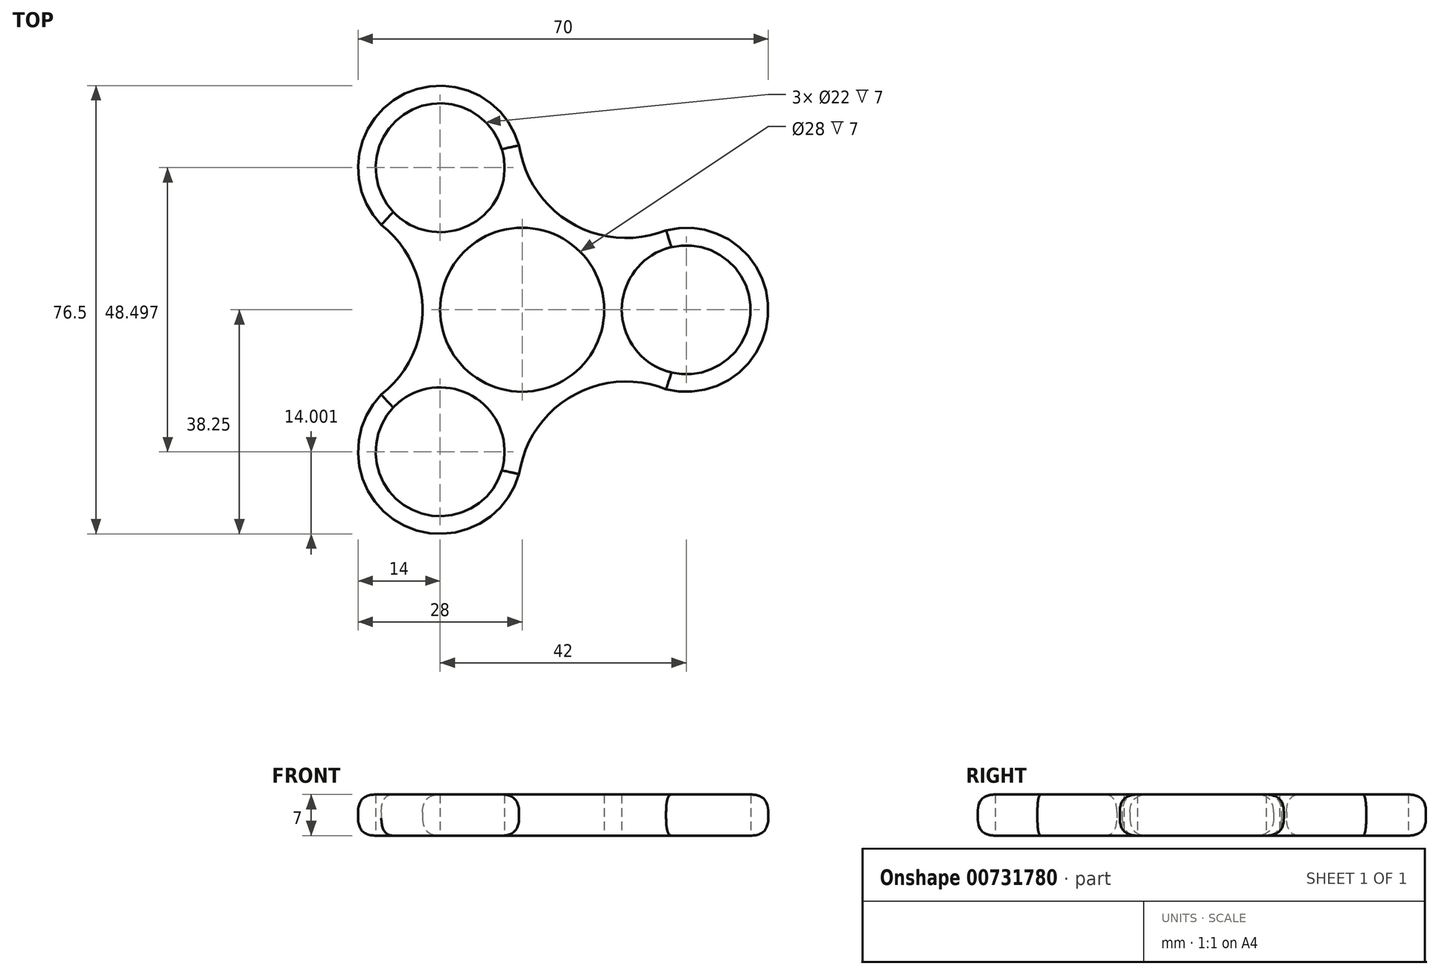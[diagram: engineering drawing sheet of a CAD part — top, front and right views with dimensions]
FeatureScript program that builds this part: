
annotation { "Feature Type Name" : "Feature", "Feature Type Description" : "" }
export const myFeature = defineFeature(function(context is Context, id is Id, definition is map)
    precondition{}
    {
        {
            var Q0;
            Q0=qCreatedBy(makeId("Top.planeOp"),FACE);
            var sketch = newSketch(context, id + "F0", { "sketchPlane" : qUnion([Q0])});
            skLineSegment(sketch, "E0", {"start": v(17, 0) * mm, "end": v(28, 0) * mm});
            skCircle(sketch, "E1", {"center": v(28, 0) * mm, "radius": 11 * mm});
            skArc(sketch, "E2", {"start": v(22.57, -12.9) * mm, "mid": v(42, 0) * mm, "end": v(22.57, 12.9) * mm});
            skPoint(sketch, "E3.center", {"position": v(0, 0) * mm});
            skArc(sketch, "E4", {"start": v(-24.03, -14.48) * mm, "mid": v(-17, 0) * mm, "end": v(-24.03, 14.48) * mm});
            skArc(sketch, "E5.1.0", {"start": v(24.56, -13.57) * mm, "mid": v(8.5, -14.72) * mm, "end": v(-0.53, -28.05) * mm});
            skArc(sketch, "E5.1.1", {"start": v(-0.1, 26) * mm, "mid": v(-21, 36.37) * mm, "end": v(-22.46, 13.1) * mm});
            skCircle(sketch, "E5.1.2", {"center": v(-14, 24.25) * mm, "radius": 11 * mm});
            skArc(sketch, "E5.2.0", {"start": v(-0.53, 28.05) * mm, "mid": v(8.5, 14.72) * mm, "end": v(24.56, 13.57) * mm});
            skArc(sketch, "E5.2.1", {"start": v(-22.46, -13.1) * mm, "mid": v(-21, -36.37) * mm, "end": v(-0.1, -26) * mm});
            skCircle(sketch, "E5.2.2", {"center": v(-14, -24.25) * mm, "radius": 11 * mm});
            skCircle(sketch, "E6", {"center": v(0, 0) * mm, "radius": 14 * mm});
            skSolve(sketch);
        }
        {
            var Q0;
            Q0=makeQuery(id+"F0.imprint","IMPRINT",FACE,{"disambiguationData":[TD([[makeQuery(id+"F0.imprint","IMPRINT",EDGE,{"derivedFrom":sQuery(id+"F0.wireOp",EDGE,"E1")}),-1.0]])]});
            extrude(context, id + "F1", {"entities" : qUnion([Q0]), "depth" : 3.5 * mm, "offsetDistance" : 25 * mm, "hasSecondDirection" : true, "secondDirectionOppositeDirection" : true, "secondDirectionDepth" : 3.5 * mm});
        }
        {
            var Q0;
            Q0=makeQuery(id+"F1.opExtrude","CAP_EDGE",EDGE,{"disambiguationData":[OSD([sQuery(id+"F0.wireOp",EDGE,"E5.1.0")])],"isStart":false});
            var Q1;
            Q1=makeQuery(id+"F1.opExtrude","CAP_EDGE",EDGE,{"disambiguationData":[OSD([sQuery(id+"F0.wireOp",EDGE,"E4")])],"isStart":false});
            var Q2;
            Q2=makeQuery(id+"F1.opExtrude","CAP_EDGE",EDGE,{"disambiguationData":[OSD([sQuery(id+"F0.wireOp",EDGE,"E5.2.0")])],"isStart":false});
            var Q3;
            Q3=makeQuery(id+"F1.opExtrude","CAP_EDGE",EDGE,{"disambiguationData":[OSD([sQuery(id+"F0.wireOp",EDGE,"E5.2.1")])],"isStart":false});
            var Q4;
            Q4=makeQuery(id+"F1.opExtrude","CAP_EDGE",EDGE,{"disambiguationData":[OSD([sQuery(id+"F0.wireOp",EDGE,"E2")])],"isStart":false});
            var Q5;
            Q5=makeQuery(id+"F1.opExtrude","CAP_EDGE",EDGE,{"disambiguationData":[OSD([sQuery(id+"F0.wireOp",EDGE,"E5.1.1")])],"isStart":false});
            var Q6;
            Q6=makeQuery(id+"F1.opExtrude","CAP_EDGE",EDGE,{"disambiguationData":[OSD([sQuery(id+"F0.wireOp",EDGE,"E5.1.0")])],"isStart":true});
            var Q7;
            Q7=makeQuery(id+"F1.opExtrude","CAP_EDGE",EDGE,{"disambiguationData":[OSD([sQuery(id+"F0.wireOp",EDGE,"E4")])],"isStart":true});
            var Q8;
            Q8=makeQuery(id+"F1.opExtrude","CAP_EDGE",EDGE,{"disambiguationData":[OSD([sQuery(id+"F0.wireOp",EDGE,"E5.2.0")])],"isStart":true});
            var Q9;
            Q9=makeQuery(id+"F1.opExtrude","CAP_EDGE",EDGE,{"disambiguationData":[OSD([sQuery(id+"F0.wireOp",EDGE,"E2")])],"isStart":true});
            var Q10;
            Q10=makeQuery(id+"F1.opExtrude","CAP_EDGE",EDGE,{"disambiguationData":[OSD([sQuery(id+"F0.wireOp",EDGE,"E5.1.1")])],"isStart":true});
            var Q11;
            Q11=makeQuery(id+"F1.opExtrude","CAP_EDGE",EDGE,{"disambiguationData":[OSD([sQuery(id+"F0.wireOp",EDGE,"E5.2.1")])],"isStart":true});
            fillet(context, id + "F2", {"entities" : qUnion([Q0, Q1, Q2, Q3, Q4, Q5, Q6, Q7, Q8, Q9, Q10, Q11]), "radius" : 3 * mm, "rho" : 0.5, "crossSection" : FilletCrossSection.CONIC, "allowEdgeOverflow" : false});
        }
    });
